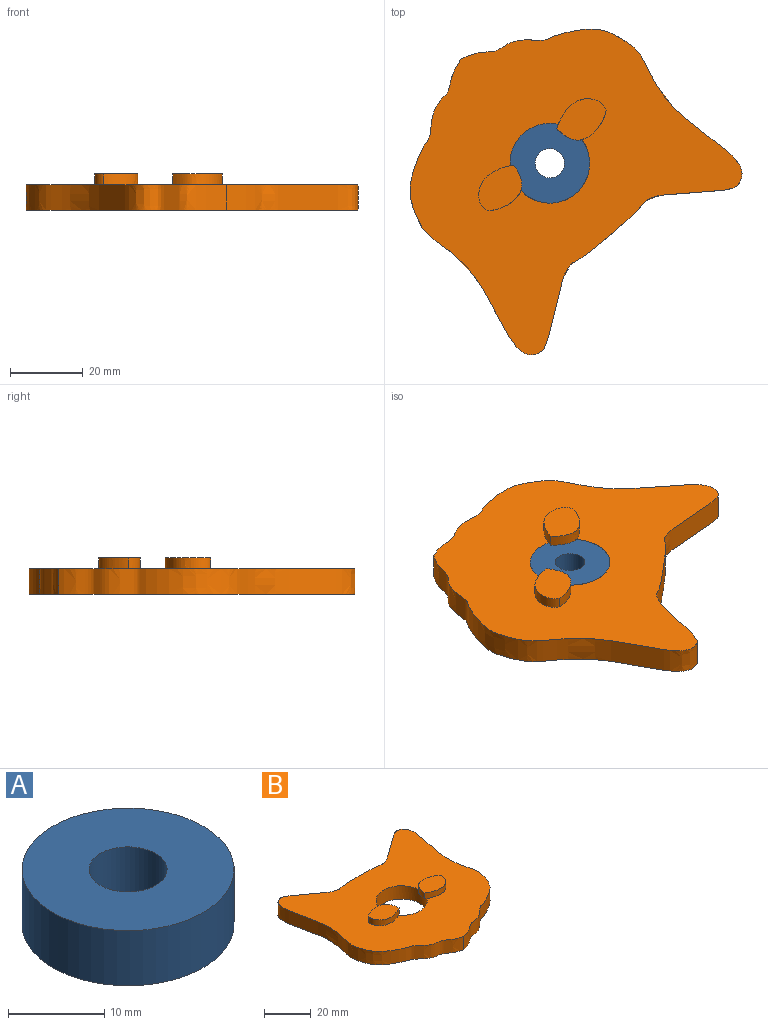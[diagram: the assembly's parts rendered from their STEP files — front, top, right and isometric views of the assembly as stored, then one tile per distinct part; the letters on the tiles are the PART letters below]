
ASSEMBLY  parts=2 mates=1
PART A: 4 faces, bbox 22x22x7 mm
  f0: cylinder r=4.05mm len=8.1mm, axis (0,0,-1), area 178.1mm2, adj f2,f3
  f1: cylinder r=11mm len=22mm, axis (0,0,-1), area 483.8mm2, adj f2,f3
  f2: plane 22x22mm, normal (0,0,1), area 328.6mm2, adj f0,f1
  f3: plane 22x22mm, normal (0,0,-1), area 328.6mm2, adj f0,f1
PART B: 13 faces, bbox 80.2x76x10 mm
  f0: plane 80.23x75.99mm, normal (0,0,1), area 3805.7mm2, adj f1,f2,f3,f5,f6,f10,f11
  f1: extruded ~75.9x39.66mm, area 981.5mm2, adj f0,f3,f4
  f2: cylinder r=11mm len=22mm, axis (0,0,-1), area 483.8mm2, adj f0,f4,f8,f9
  f3: extruded ~75.9x39.66mm, area 981.5mm2, adj f0,f1,f4
  f4: plane 80.23x75.99mm, normal (0,0,-1), area 3995.2mm2, adj f1,f2,f3
  f5: extruded ~14.07x7.34mm, area 57.7mm2, adj f0,f6,f7,f8
  f6: extruded ~13.7x7.38mm, area 56.6mm2, adj f0,f5,f7,f8
  f7: plane 14.43x10.53mm, normal (0,0,1), area 107.4mm2, adj f5,f6
  f8: plane 7.65x3.6mm, normal (0,0,-1), area 13.7mm2, adj f2,f5,f6
  f9: plane 7.39x3.31mm, normal (0,0,-1), area 11.6mm2, adj f2,f10,f11
  f10: extruded ~14.07x7.34mm, area 57.7mm2, adj f0,f9,f11,f12
  f11: extruded ~13.7x7.38mm, area 56.6mm2, adj f0,f9,f10,f12
  f12: plane 14.43x10.53mm, normal (0,0,1), area 107.4mm2, adj f10,f11
PLACE A t=(-21.04,-12.99,-4.44)mm fixed
PLACE B rot(axis=(0,0,-1),139.7deg) t=(-21.04,-12.99,-4.44)mm
MATE revolute B.f2 <-> A.f0  axis (0,0,-1) through (-21.04,-12.99,2.56)mm
